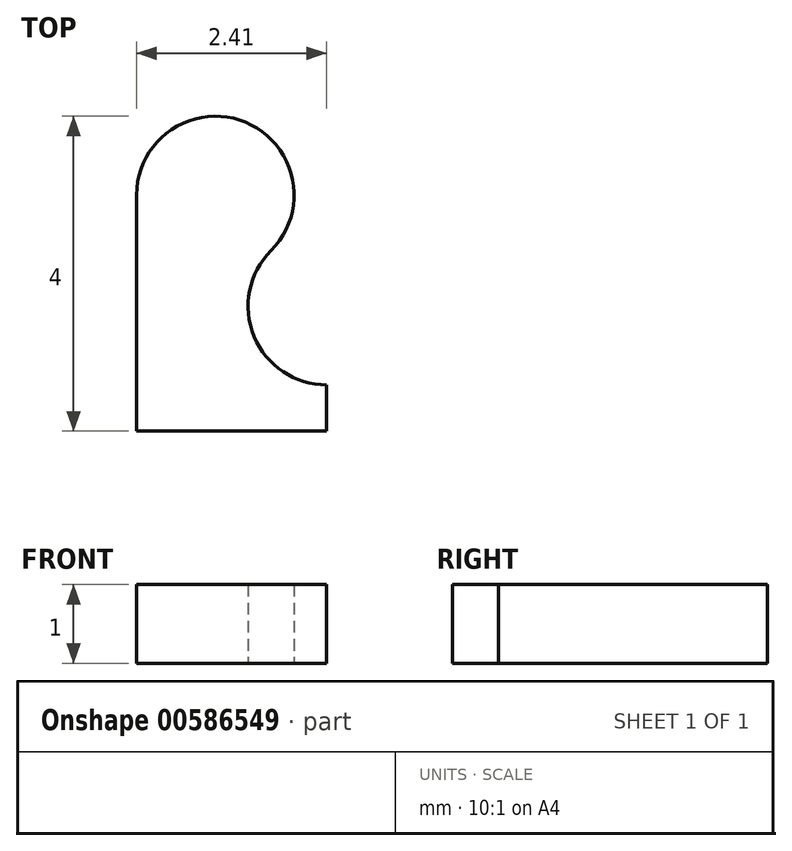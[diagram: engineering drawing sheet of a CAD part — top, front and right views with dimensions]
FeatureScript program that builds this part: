
annotation { "Feature Type Name" : "Feature", "Feature Type Description" : "" }
export const myFeature = defineFeature(function(context is Context, id is Id, definition is map)
    precondition{}
    {
        {
            var Q0;
            Q0=qCreatedBy(makeId("Top.planeOp"),FACE);
            var sketch = newSketch(context, id + "F0", { "sketchPlane" : qUnion([Q0])});
            skLineSegment(sketch, "E0", {"start": v(0, 0) * mm, "end": v(0, 3) * mm});
            skArc(sketch, "E1", {"start": v(0, 3) * mm, "mid": v(1.38, 3.92) * mm, "end": v(1.7, 2.3) * mm});
            skArc(sketch, "E2", {"start": v(1.7, 2.3) * mm, "mid": v(1.5, 1.2) * mm, "end": v(2.41, 0.59) * mm});
            skLineSegment(sketch, "E3", {"start": v(1, 3) * mm, "end": v(2.41, 1.59) * mm, "construction": true});
            skLineSegment(sketch, "E4", {"start": v(2.41, 0) * mm, "end": v(2.41, 1.59) * mm, "construction": true});
            skLineSegment(sketch, "E5", {"start": v(0, 0) * mm, "end": v(2.41, 0) * mm});
            skLineSegment(sketch, "E6", {"start": v(2.41, 0.59) * mm, "end": v(2.41, 0) * mm});
            skLineSegment(sketch, "E7", {"start": v(0, 3) * mm, "end": v(1, 3) * mm, "construction": true});
            skLineSegment(sketch, "E8", {"start": v(1, 3) * mm, "end": v(1, 2) * mm, "construction": true});
            skLineSegment(sketch, "E9", {"start": v(1, 2) * mm, "end": v(1, 1) * mm, "construction": true});
            skLineSegment(sketch, "E10", {"start": v(1, 0) * mm, "end": v(1, 1) * mm, "construction": true});
            skSolve(sketch);
        }
        {
            var Q0;
            Q0 = qSketchRegion(id + "F0", true);
            extrude(context, id + "F1", {"entities" : qUnion([Q0]), "depth" : 1 * mm, "offsetDistance" : 25 * mm});
        }
    });
